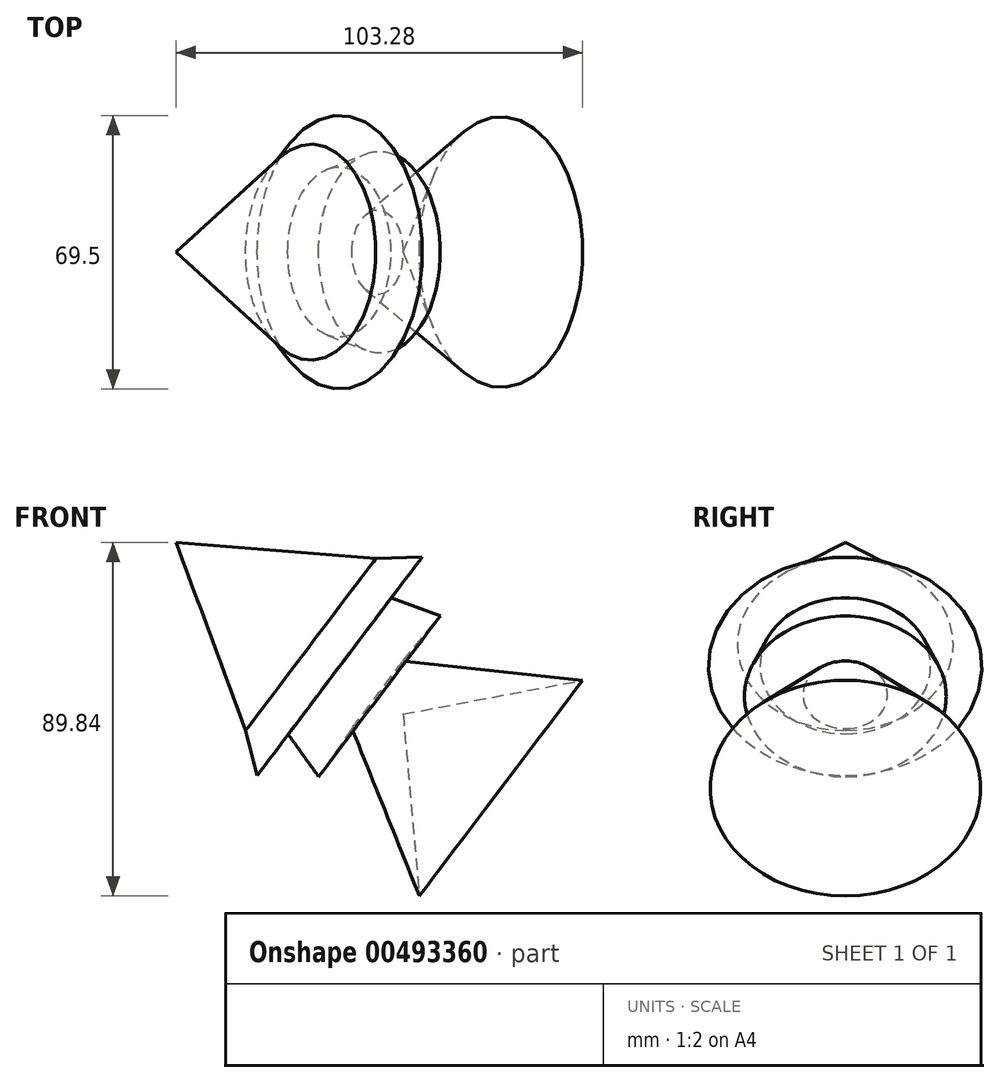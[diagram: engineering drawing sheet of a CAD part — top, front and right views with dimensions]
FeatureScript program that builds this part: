
annotation { "Feature Type Name" : "Feature", "Feature Type Description" : "" }
export const myFeature = defineFeature(function(context is Context, id is Id, definition is map)
    precondition{}
    {
        {
            var Q0;
            Q0=qCreatedBy(makeId("Front.planeOp"),FACE);
            var sketch = newSketch(context, id + "F0", { "sketchPlane" : qUnion([Q0])});
            skLineSegment(sketch, "E0", {"start": v(-19.5, 17.64) * mm, "end": v(-7.75, 17.93) * mm});
            skLineSegment(sketch, "E1", {"start": v(-7.75, 17.93) * mm, "end": v(-15.78, 7.6) * mm});
            skLineSegment(sketch, "E2", {"start": v(-15.78, 7.6) * mm, "end": v(-3.16, 3.01) * mm});
            skLineSegment(sketch, "E3", {"start": v(-3.16, 3.01) * mm, "end": v(-12.62, -8.46) * mm});
            skLineSegment(sketch, "E4", {"start": v(-12.62, -8.46) * mm, "end": v(33, -13.34) * mm});
            skLineSegment(sketch, "E5", {"start": v(33, -13.34) * mm, "end": v(-12.62, -21.95) * mm});
            skLineSegment(sketch, "E6", {"start": v(-12.62, -21.95) * mm, "end": v(-70.29, 21.66) * mm});
            skLineSegment(sketch, "E7", {"start": v(-70.29, 21.66) * mm, "end": v(-19.5, 17.64) * mm});
            skSolve(sketch);
        }
        {
            var Q0;
            Q0=makeQuery(id+"F0.imprint","IMPRINT",FACE,{"disambiguationData":[TD([[makeQuery(id+"F0.imprint","IMPRINT",EDGE,{"derivedFrom":sQuery(id+"F0.wireOp",EDGE,"E0")}),-1.0]])]});
            var Q1;
            Q1=sQuery(id+"F0.wireOp",EDGE,"E6");
            revolve(context, id + "F1", {"entities" : qUnion([Q0]), "axis" : qUnion([Q1]), "revolveType" : RevolveType.FULL});
        }
    });
